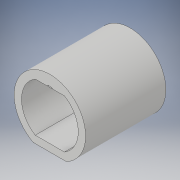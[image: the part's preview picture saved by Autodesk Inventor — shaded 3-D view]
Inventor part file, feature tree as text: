
AUTODESK INVENTOR PART (.ipt)
format: ipt  version: 2017 (Build 210142000, 142)  size: 144,896 bytes
history: native  units: in
note: dims shown in document units (in); Inventor stores cm internally (conversion verified against a paired STEP export)
features: sketch x2, other x1, extrude x1
ambient origin geometry x8: Origin, YZ Plane, XZ Plane, XY Plane, X Axis, Y Axis, Z Axis, Center Point
bodies: Solid1 (feature_tree), Solid2 (feature_tree)
feature tree (4):
  other  "corridor"
  extrude  "light"  Depth=1.0in TaperAngle=0.0deg
  sketch  "Sketch1"  dims[d0=6.6667in d1=4.0in d2=1.0in d3=11.0in d4=0.0in]
  sketch  "Sketch5"  dims[d7=1.0in d20=1.0in d21=4.8944in d23=0.5833in d26=0.125in d27=3.8873in d28=3.8873in d30=1.7083in d31=0.25in d32=0.125in d34=45.0deg d35=0.0892in d36=0.0884in d37=1.0in d38=0.0in d39=0.0625in d40=0.0625in d41=1.6458in d44=0.125in d45=0.0482in]
